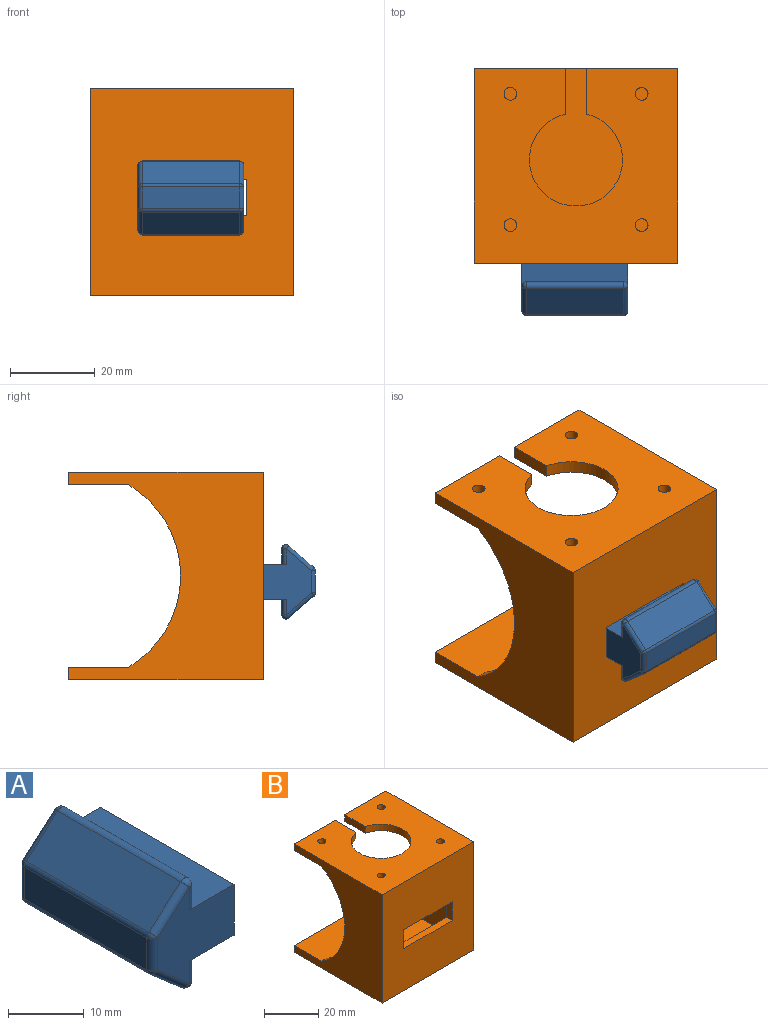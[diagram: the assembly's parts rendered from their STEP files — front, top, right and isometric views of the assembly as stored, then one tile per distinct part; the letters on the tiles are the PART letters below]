
ASSEMBLY  parts=2 mates=1
PART A: 32 faces, bbox 15.3x25x17.6 mm
  f0: plane 25x8.25mm, normal (1,0,0), area 206.3mm2, adj f1,f7,f8,f9
  f1: plane 25x8.35mm, normal (0,0,1), area 184.2mm2, adj f0,f2,f8,f9,f25,f28
  f2: plane 23x3.67mm, normal (1,0,0), area 84.5mm2, adj f1,f25,f28,f31
  f3: plane 23x5.95mm, normal (-0.66,0,0.75), area 181.8mm2, adj f21,f26,f27,f31
  f4: plane 23x5.19mm, normal (-1,0,0), area 119.4mm2, adj f16,f20,f21,f22
  f5: plane 23x5.95mm, normal (-0.66,0,-0.75), area 181.8mm2, adj f11,f15,f16,f17
  f6: plane 23x3.67mm, normal (1,0,0), area 84.5mm2, adj f7,f10,f11,f12
  f7: plane 25x8.35mm, normal (0,0,-1), area 184.2mm2, adj f0,f6,f8,f9,f10,f12
  f8: plane 15.59x14.3mm, normal (0,-1,0), area 130.7mm2, adj f0,f1,f7,f10,f15,f20,f25,f26
  f9: plane 15.59x14.3mm, normal (0,1,0), area 130.7mm2, adj f0,f1,f7,f12,f17,f22,f27,f28
  f10: cylinder r=1mm len=3.67mm, axis (0,0,-1), area 5.8mm2, adj f6,f7,f8,f13
  f11: cylinder r=1mm len=23mm, axis (0,1,0), area 52.7mm2, adj f5,f6,f13,f14
  f12: cylinder r=1mm len=3.67mm, axis (0,0,1), area 5.8mm2, adj f6,f7,f9,f14
  f13: sphere r=1mm, area 2.3mm2, adj f10,f11,f15
  f14: sphere r=1mm, area 2.3mm2, adj f11,f12,f17
  f15: cylinder r=1mm len=6.61mm, axis (-0.75,0,0.66), area 12.4mm2, adj f5,f8,f13,f18
  f16: cylinder r=1mm len=23mm, axis (0,-1,0), area 19.6mm2, adj f4,f5,f18,f19
  f17: cylinder r=1mm len=6.61mm, axis (0.75,0,-0.66), area 12.4mm2, adj f5,f9,f14,f19
  f18: sphere r=1mm, area 0.9mm2, adj f15,f16,f20
  f19: sphere r=1mm, area 0.9mm2, adj f16,f17,f22
  f20: cylinder r=1mm len=5.19mm, axis (0,0,1), area 8.2mm2, adj f4,f8,f18,f23
  f21: cylinder r=1mm len=23mm, axis (0,1,0), area 19.6mm2, adj f3,f4,f23,f24
  f22: cylinder r=1mm len=5.19mm, axis (0,0,-1), area 8.2mm2, adj f4,f9,f19,f24
  f23: sphere r=1mm, area 0.9mm2, adj f20,f21,f26
  f24: sphere r=1mm, area 0.9mm2, adj f21,f22,f27
  f25: cylinder r=1mm len=3.67mm, axis (0,0,-1), area 5.8mm2, adj f1,f2,f8,f29
  f26: cylinder r=1mm len=6.61mm, axis (0.75,0,0.66), area 12.4mm2, adj f3,f8,f23,f29
  f27: cylinder r=1mm len=6.61mm, axis (-0.75,0,-0.66), area 12.4mm2, adj f3,f9,f24,f30
  f28: cylinder r=1mm len=3.67mm, axis (0,0,1), area 5.8mm2, adj f1,f2,f9,f30
  f29: sphere r=1mm, area 2.3mm2, adj f25,f26,f31
  f30: sphere r=1mm, area 2.3mm2, adj f27,f28,f31
  f31: cylinder r=1mm len=23mm, axis (0,1,0), area 52.7mm2, adj f2,f3,f29,f30
PART B: 26 faces, bbox 48x46x49 mm
  f0: plane 43x43mm, normal (0,1,0), area 1632.2mm2, adj f3,f4,f11,f13,f22,f23,f24,f25
  f1: plane 49x48mm, normal (0,-1,0), area 2135.2mm2, adj f5,f6,f9,f10,f22,f23,f24,f25
  f2: plane 21.5x3mm, normal (0,1,0), area 64.5mm2, adj f3,f5,f10,f16
  f3: plane 48x43mm, normal (0,0,-1), area 1458.7mm2, adj f0,f2,f8,f9,f10,f11,f12,f13
  f4: plane 48x43mm, normal (0,0,1), area 1920.1mm2, adj f0,f7,f9,f10,f11,f12,f13,f14
  f5: plane 48x46mm, normal (0,0,1), area 1746.6mm2, adj f1,f2,f8,f9,f10,f15,f16,f17
  f6: plane 48x46mm, normal (0,0,-1), area 2208mm2, adj f1,f7,f9,f10
  f7: plane 48x3mm, normal (0,1,0), area 144mm2, adj f4,f6,f9,f10
  f8: plane 21.5x3mm, normal (0,1,0), area 64.5mm2, adj f3,f5,f9,f15
  f9: plane 49x46mm, normal (1,0,0), area 1269.8mm2, adj f1,f3,f4,f5,f6,f7,f8,f12
  f10: plane 49x46mm, normal (-1,0,0), area 1269.8mm2, adj f1,f2,f3,f4,f5,f6,f7,f14
  f11: plane 43x28.78mm, normal (-1,0,0), area 864.8mm2, adj f0,f3,f4,f12
  f12: cylinder r=25mm len=43mm, axis (1,0,0), area 129.4mm2, adj f3,f4,f9,f11
  f13: plane 43x28.78mm, normal (1,0,0), area 864.8mm2, adj f0,f3,f4,f14
  f14: cylinder r=25mm len=43mm, axis (-1,0,0), area 129.4mm2, adj f3,f4,f10,f13
  f15: plane 10.79x3mm, normal (-1,0,0), area 32.4mm2, adj f3,f5,f8,f17
  f16: plane 10.79x3mm, normal (1,0,0), area 32.4mm2, adj f2,f3,f5,f17
  f17: cylinder r=11mm len=22mm, axis (0,0,1), area 192.2mm2, adj f3,f5,f15,f16
  f18: cylinder r=1.5mm len=3mm, axis (0,0,1), area 28.3mm2, adj f3,f5
  f19: cylinder r=1.5mm len=3mm, axis (0,0,1), area 28.3mm2, adj f3,f5
  f20: cylinder r=1.5mm len=3mm, axis (0,0,1), area 28.3mm2, adj f3,f5
  f21: cylinder r=1.5mm len=3mm, axis (0,0,1), area 28.3mm2, adj f3,f5
  f22: plane 25.5x3mm, normal (0,0,-1), area 76.5mm2, adj f0,f1,f23,f25
  f23: plane 8.5x3mm, normal (1,0,0), area 25.5mm2, adj f0,f1,f22,f24
  f24: plane 25.5x3mm, normal (0,0,1), area 76.5mm2, adj f0,f1,f23,f25
  f25: plane 8.5x3mm, normal (-1,0,0), area 25.5mm2, adj f0,f1,f22,f24
PLACE A rot(axis=(0,0,1),90deg) t=(2.64,-22.16,1.76)mm
PLACE B t=(2.89,6.62,3.01)mm fixed
MATE fastened A.f0 <-> B.f0  axis (0,1,0) through (-9.86,-22.16,1.76)mm
